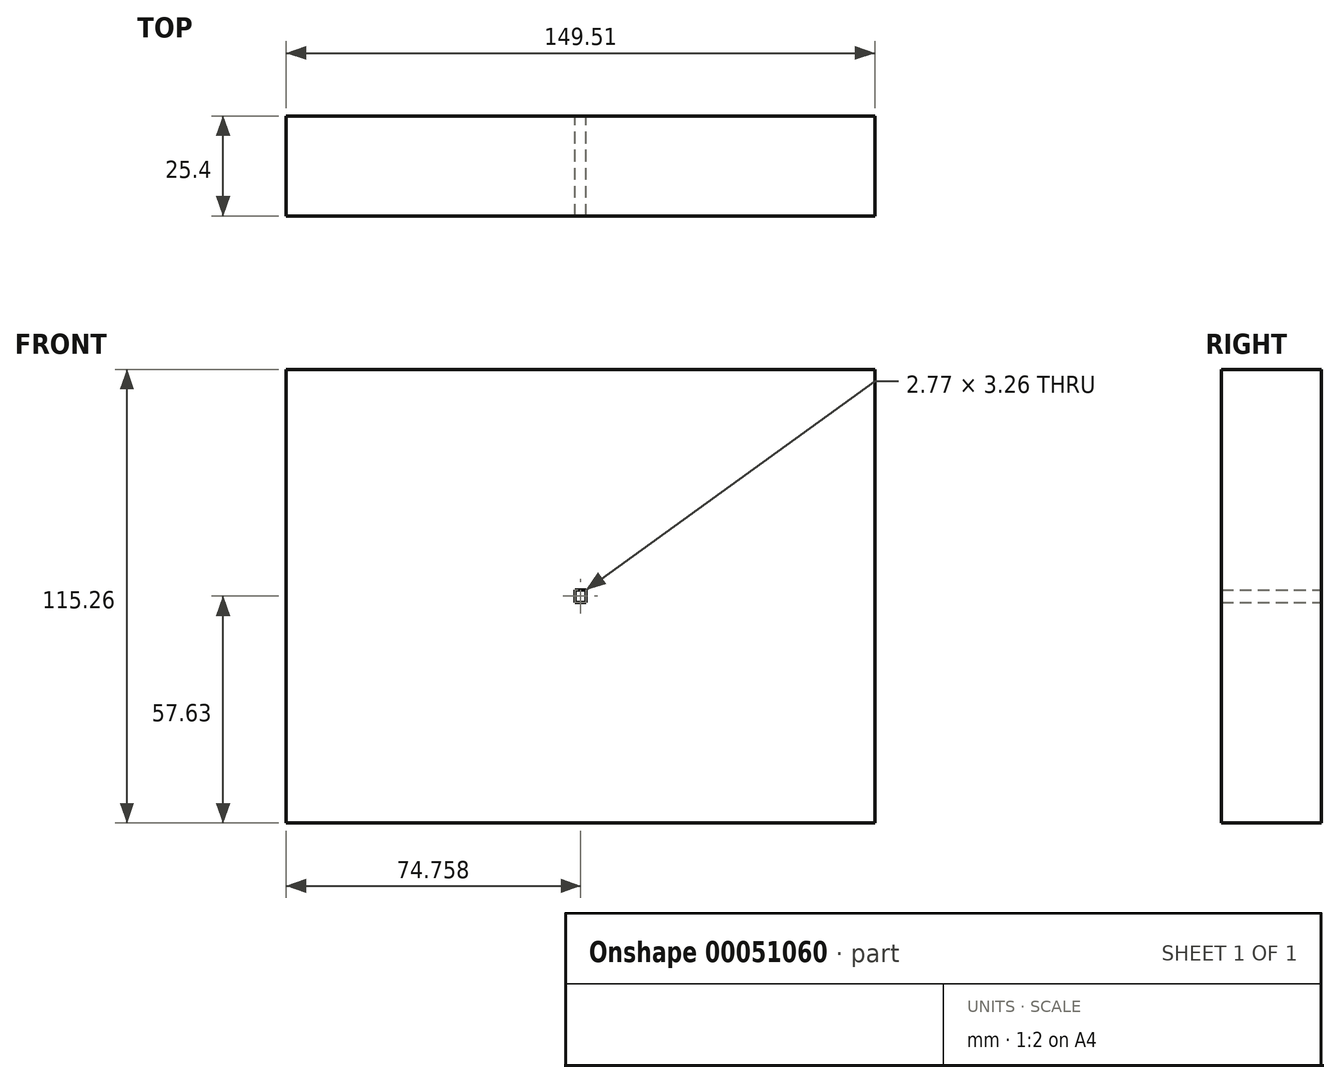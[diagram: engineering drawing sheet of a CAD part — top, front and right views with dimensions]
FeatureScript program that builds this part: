
annotation { "Feature Type Name" : "Feature", "Feature Type Description" : "" }
export const myFeature = defineFeature(function(context is Context, id is Id, definition is map)
    precondition{}
    {
        {
            var Q0;
            Q0=qCreatedBy(makeId("Front.planeOp"),FACE);
            var sketch = newSketch(context, id + "F0", { "sketchPlane" : qUnion([Q0])});
            skLineSegment(sketch, "E0.top", {"start": v(13.5, 0) * mm, "end": v(-11.5, 0) * mm});
            skLineSegment(sketch, "E1.rect.bottom", {"start": v(13.5, -2.63) * mm, "end": v(-16.33, -2.63) * mm});
            skLineSegment(sketch, "E1.rect.top", {"start": v(13.5, -26.63) * mm, "end": v(-16.33, -26.63) * mm});
            skLineSegment(sketch, "E1.rect.left", {"start": v(13.5, -2.63) * mm, "end": v(13.5, -26.63) * mm});
            skLineSegment(sketch, "E1.rect.right", {"start": v(-16.33, -2.63) * mm, "end": v(-16.33, -26.63) * mm});
            skPoint(sketch, "E1.rect.middle", {"position": v(-1.41, -14.63) * mm});
            skLineSegment(sketch, "E2.rect.bottom", {"start": v(20.55, 0) * mm, "end": v(-23.37, 0) * mm});
            skLineSegment(sketch, "E2.rect.top", {"start": v(20.55, -29.26) * mm, "end": v(-23.37, -29.26) * mm});
            skLineSegment(sketch, "E2.rect.left", {"start": v(20.55, 0) * mm, "end": v(20.55, -29.26) * mm});
            skLineSegment(sketch, "E2.rect.right", {"start": v(-23.37, 0) * mm, "end": v(-23.37, -29.26) * mm});
            skLineSegment(sketch, "E3.rect.bottom", {"start": v(34.9, 9.79) * mm, "end": v(-37.73, 9.79) * mm});
            skLineSegment(sketch, "E3.rect.top", {"start": v(34.9, -39.05) * mm, "end": v(-37.73, -39.05) * mm});
            skLineSegment(sketch, "E3.rect.left", {"start": v(34.9, 9.79) * mm, "end": v(34.9, -39.05) * mm});
            skLineSegment(sketch, "E3.rect.right", {"start": v(-37.73, 9.79) * mm, "end": v(-37.73, -39.05) * mm});
            skLineSegment(sketch, "E4.rect.bottom", {"start": v(44.2, 15.84) * mm, "end": v(-47.02, 15.84) * mm});
            skLineSegment(sketch, "E4.rect.top", {"start": v(44.2, -45.1) * mm, "end": v(-47.02, -45.1) * mm});
            skLineSegment(sketch, "E4.rect.left", {"start": v(44.2, 15.84) * mm, "end": v(44.2, -45.1) * mm});
            skLineSegment(sketch, "E4.rect.right", {"start": v(-47.02, 15.84) * mm, "end": v(-47.02, -45.1) * mm});
            skLineSegment(sketch, "E5.rect.bottom", {"start": v(53.88, 23.91) * mm, "end": v(-56.7, 23.91) * mm});
            skLineSegment(sketch, "E5.rect.top", {"start": v(53.88, -53.17) * mm, "end": v(-56.7, -53.17) * mm});
            skLineSegment(sketch, "E5.rect.left", {"start": v(53.88, 23.91) * mm, "end": v(53.88, -53.17) * mm});
            skLineSegment(sketch, "E5.rect.right", {"start": v(-56.7, 23.91) * mm, "end": v(-56.7, -53.17) * mm});
            skLineSegment(sketch, "E6.rect.bottom", {"start": v(63.97, 33.2) * mm, "end": v(-66.8, 33.2) * mm});
            skLineSegment(sketch, "E6.rect.top", {"start": v(63.97, -62.45) * mm, "end": v(-66.8, -62.45) * mm});
            skLineSegment(sketch, "E6.rect.left", {"start": v(63.97, 33.2) * mm, "end": v(63.97, -62.45) * mm});
            skLineSegment(sketch, "E6.rect.right", {"start": v(-66.8, 33.2) * mm, "end": v(-66.8, -62.45) * mm});
            skLineSegment(sketch, "E7.rect.bottom", {"start": v(73.34, 43) * mm, "end": v(-76.17, 43) * mm});
            skLineSegment(sketch, "E7.rect.top", {"start": v(73.34, -72.26) * mm, "end": v(-76.17, -72.26) * mm});
            skLineSegment(sketch, "E7.rect.left", {"start": v(73.34, 43) * mm, "end": v(73.34, -72.26) * mm});
            skLineSegment(sketch, "E7.rect.right", {"start": v(-76.17, 43) * mm, "end": v(-76.17, -72.26) * mm});
            skLineSegment(sketch, "E8", {"start": v(-76.17, 43) * mm, "end": v(-23.37, 0) * mm});
            skLineSegment(sketch, "E9", {"start": v(34.9, 9.79) * mm, "end": v(73.34, 43) * mm});
            skLineSegment(sketch, "E10", {"start": v(-23.37, -29.26) * mm, "end": v(-76.17, -72.26) * mm});
            skLineSegment(sketch, "E11", {"start": v(20.55, -29.26) * mm, "end": v(73.34, -72.26) * mm});
            skLineSegment(sketch, "E12", {"start": v(34.9, 9.79) * mm, "end": v(20.55, 0) * mm});
            skLineSegment(sketch, "E13", {"start": v(-23.37, -29.26) * mm, "end": v(-16.33, -26.63) * mm});
            skLineSegment(sketch, "E14", {"start": v(20.55, -29.26) * mm, "end": v(13.5, -26.63) * mm});
            skLineSegment(sketch, "E15", {"start": v(13.5, -2.63) * mm, "end": v(20.55, 0) * mm});
            skLineSegment(sketch, "E16", {"start": v(-16.33, -2.63) * mm, "end": v(-23.37, 0) * mm});
            skLineSegment(sketch, "E17.rect.bottom", {"start": v(5, -8.29) * mm, "end": v(-7.82, -8.29) * mm});
            skLineSegment(sketch, "E17.rect.top", {"start": v(5, -20.97) * mm, "end": v(-7.82, -20.97) * mm});
            skLineSegment(sketch, "E17.rect.left", {"start": v(5, -8.29) * mm, "end": v(5, -20.97) * mm});
            skLineSegment(sketch, "E17.rect.right", {"start": v(-7.82, -8.29) * mm, "end": v(-7.82, -20.97) * mm});
            skLineSegment(sketch, "E18", {"start": v(13.5, -26.63) * mm, "end": v(5, -20.97) * mm});
            skLineSegment(sketch, "E19", {"start": v(-16.33, -26.63) * mm, "end": v(-7.82, -20.97) * mm});
            skLineSegment(sketch, "E20", {"start": v(13.5, -2.63) * mm, "end": v(5, -8.29) * mm});
            skLineSegment(sketch, "E21", {"start": v(-1.61, -10.6) * mm, "end": v(-16.33, -2.63) * mm});
            skLineSegment(sketch, "E22.rect.bottom", {"start": v(-0.03, -13) * mm, "end": v(-2.8, -13) * mm});
            skLineSegment(sketch, "E22.rect.top", {"start": v(-0.03, -16.26) * mm, "end": v(-2.8, -16.26) * mm});
            skLineSegment(sketch, "E22.rect.left", {"start": v(-0.03, -13) * mm, "end": v(-0.03, -16.26) * mm});
            skLineSegment(sketch, "E22.rect.right", {"start": v(-2.8, -13) * mm, "end": v(-2.8, -16.26) * mm});
            skLineSegment(sketch, "E23", {"start": v(5, -20.97) * mm, "end": v(-0.03, -16.26) * mm});
            skLineSegment(sketch, "E24", {"start": v(-7.82, -20.97) * mm, "end": v(-2.8, -16.26) * mm});
            skLineSegment(sketch, "E25", {"start": v(-7.82, -8.29) * mm, "end": v(-2.8, -13) * mm});
            skLineSegment(sketch, "E26", {"start": v(5, -8.29) * mm, "end": v(-0.03, -13) * mm});
            skSolve(sketch);
        }
        {
            var Q0;
            {var subQ1=sQuery(id+"F0.wireOp",EDGE,"E6.rect.right");Q0=makeQuery(id+"F0.imprint","IMPRINT",FACE,{"disambiguationData":[TD([[makeQuery(id+"F0.imprint","IMPRINT",EDGE,{"derivedFrom":subQ1}),-1.0]])]});}
            var Q1;
            {var subQ5=sQuery(id+"F0.wireOp",EDGE,"E7.rect.bottom");Q1=makeQuery(id+"F0.imprint","IMPRINT",FACE,{"disambiguationData":[TD([[makeQuery(id+"F0.imprint","IMPRINT",EDGE,{"derivedFrom":subQ5}),1.0]])]});}
            var Q2;
            {var subQ1=sQuery(id+"F0.wireOp",EDGE,"E6.rect.left");Q2=makeQuery(id+"F0.imprint","IMPRINT",FACE,{"disambiguationData":[TD([[makeQuery(id+"F0.imprint","IMPRINT",EDGE,{"derivedFrom":subQ1}),1.0]])]});}
            var Q3;
            {var subQ5=sQuery(id+"F0.wireOp",EDGE,"E7.rect.top");Q3=makeQuery(id+"F0.imprint","IMPRINT",FACE,{"disambiguationData":[TD([[makeQuery(id+"F0.imprint","IMPRINT",EDGE,{"derivedFrom":subQ5}),-1.0]])]});}
            extrude(context, id + "F1", {"entities" : qUnion([Q0, Q1, Q2, Q3]), "depth" : 25.4 * mm});
        }
        {
            var Q0;
            {var subQ4=sQuery(id+"F0.wireOp",EDGE,"E5.rect.right");Q0=makeQuery(id+"F0.imprint","IMPRINT",FACE,{"disambiguationData":[TD([[makeQuery(id+"F0.imprint","IMPRINT",EDGE,{"derivedFrom":subQ4}),-1.0]])]});}
            var Q1;
            {var subQ0=sQuery(id+"F0.wireOp",EDGE,"E9");var subQ1=sQuery(id+"F0.wireOp",EDGE,"E5.rect.bottom");var subQ2=makeQuery(id+"F0.imprint","INTERSECT",VERTEX,{"derivedFrom":[subQ1,subQ0]});Q1=makeQuery(id+"F0.imprint","IMPRINT",FACE,{"disambiguationData":[TD([[makeQuery(id+"F0.imprint","IMPRINT",EDGE,{"disambiguationData":[TD([[subQ2,-1.0]])],"derivedFrom":subQ1}),-1.0]])]});}
            var Q2;
            {var subQ4=sQuery(id+"F0.wireOp",EDGE,"E5.rect.left");Q2=makeQuery(id+"F0.imprint","IMPRINT",FACE,{"disambiguationData":[TD([[makeQuery(id+"F0.imprint","IMPRINT",EDGE,{"derivedFrom":subQ4}),1.0]])]});}
            var Q3;
            {var subQ0=sQuery(id+"F0.wireOp",EDGE,"E11");var subQ1=sQuery(id+"F0.wireOp",EDGE,"E5.rect.top");var subQ2=makeQuery(id+"F0.imprint","INTERSECT",VERTEX,{"derivedFrom":[subQ1,subQ0]});Q3=makeQuery(id+"F0.imprint","IMPRINT",FACE,{"disambiguationData":[TD([[makeQuery(id+"F0.imprint","IMPRINT",EDGE,{"disambiguationData":[TD([[subQ2,-1.0]])],"derivedFrom":subQ1}),1.0]])]});}
            extrude(context, id + "F2", {"entities" : qUnion([Q0, Q1, Q2, Q3]), "operationType" : NewBodyOperationType.ADD, "depth" : 25.4 * mm});
        }
        {
            var Q0;
            {var subQ4=sQuery(id+"F0.wireOp",EDGE,"E4.rect.right");Q0=makeQuery(id+"F0.imprint","IMPRINT",FACE,{"disambiguationData":[TD([[makeQuery(id+"F0.imprint","IMPRINT",EDGE,{"derivedFrom":subQ4}),-1.0]])]});}
            var Q1;
            {var subQ0=sQuery(id+"F0.wireOp",EDGE,"E9");var subQ1=sQuery(id+"F0.wireOp",EDGE,"E4.rect.bottom");var subQ2=makeQuery(id+"F0.imprint","INTERSECT",VERTEX,{"derivedFrom":[subQ1,subQ0]});Q1=makeQuery(id+"F0.imprint","IMPRINT",FACE,{"disambiguationData":[TD([[makeQuery(id+"F0.imprint","IMPRINT",EDGE,{"disambiguationData":[TD([[subQ2,-1.0]])],"derivedFrom":subQ1}),-1.0]])]});}
            var Q2;
            {var subQ4=sQuery(id+"F0.wireOp",EDGE,"E4.rect.left");Q2=makeQuery(id+"F0.imprint","IMPRINT",FACE,{"disambiguationData":[TD([[makeQuery(id+"F0.imprint","IMPRINT",EDGE,{"derivedFrom":subQ4}),1.0]])]});}
            var Q3;
            {var subQ0=sQuery(id+"F0.wireOp",EDGE,"E11");var subQ1=sQuery(id+"F0.wireOp",EDGE,"E4.rect.top");var subQ2=makeQuery(id+"F0.imprint","INTERSECT",VERTEX,{"derivedFrom":[subQ1,subQ0]});Q3=makeQuery(id+"F0.imprint","IMPRINT",FACE,{"disambiguationData":[TD([[makeQuery(id+"F0.imprint","IMPRINT",EDGE,{"disambiguationData":[TD([[subQ2,-1.0]])],"derivedFrom":subQ1}),1.0]])]});}
            extrude(context, id + "F3", {"entities" : qUnion([Q0, Q1, Q2, Q3]), "operationType" : NewBodyOperationType.ADD, "depth" : 25.4 * mm});
        }
        {
            var Q0;
            {var subQ4=sQuery(id+"F0.wireOp",EDGE,"E3.rect.right");Q0=makeQuery(id+"F0.imprint","IMPRINT",FACE,{"disambiguationData":[TD([[makeQuery(id+"F0.imprint","IMPRINT",EDGE,{"derivedFrom":subQ4}),-1.0]])]});}
            var Q1;
            {var subQ0=sQuery(id+"F0.wireOp",EDGE,"E9");var subQ5=sQuery(id+"F0.wireOp",EDGE,"E4.rect.bottom");var subQ6=makeQuery(id+"F0.imprint","INTERSECT",VERTEX,{"derivedFrom":[subQ5,subQ0]});Q1=makeQuery(id+"F0.imprint","IMPRINT",FACE,{"disambiguationData":[TD([[makeQuery(id+"F0.imprint","IMPRINT",EDGE,{"disambiguationData":[TD([[subQ6,-1.0]])],"derivedFrom":subQ5}),1.0]])]});}
            var Q2;
            {var subQ7=sQuery(id+"F0.wireOp",EDGE,"E3.rect.left");Q2=makeQuery(id+"F0.imprint","IMPRINT",FACE,{"disambiguationData":[TD([[makeQuery(id+"F0.imprint","IMPRINT",EDGE,{"derivedFrom":subQ7}),1.0]])]});}
            var Q3;
            {var subQ0=sQuery(id+"F0.wireOp",EDGE,"E11");var subQ1=sQuery(id+"F0.wireOp",EDGE,"E3.rect.top");var subQ2=makeQuery(id+"F0.imprint","INTERSECT",VERTEX,{"derivedFrom":[subQ1,subQ0]});Q3=makeQuery(id+"F0.imprint","IMPRINT",FACE,{"disambiguationData":[TD([[makeQuery(id+"F0.imprint","IMPRINT",EDGE,{"disambiguationData":[TD([[subQ2,-1.0]])],"derivedFrom":subQ1}),1.0]])]});}
            extrude(context, id + "F4", {"entities" : qUnion([Q0, Q1, Q2, Q3]), "operationType" : NewBodyOperationType.ADD, "depth" : 25.4 * mm});
        }
        {
            var Q0;
            {var subQ7=sQuery(id+"F0.wireOp",EDGE,"E2.rect.right");Q0=makeQuery(id+"F0.imprint","IMPRINT",FACE,{"disambiguationData":[TD([[makeQuery(id+"F0.imprint","IMPRINT",EDGE,{"derivedFrom":subQ7}),-1.0]])]});}
            var Q1;
            {var subQ0=sQuery(id+"F0.wireOp",EDGE,"E12");Q1=makeQuery(id+"F0.imprint","IMPRINT",FACE,{"disambiguationData":[TD([[makeQuery(id+"F0.imprint","IMPRINT",EDGE,{"derivedFrom":subQ0}),-1.0]])]});}
            var Q2;
            {var subQ1=sQuery(id+"F0.wireOp",EDGE,"E2.rect.left");Q2=makeQuery(id+"F0.imprint","IMPRINT",FACE,{"disambiguationData":[TD([[makeQuery(id+"F0.imprint","IMPRINT",EDGE,{"derivedFrom":subQ1}),1.0]])]});}
            var Q3;
            {var subQ0=sQuery(id+"F0.wireOp",EDGE,"E2.rect.top");Q3=makeQuery(id+"F0.imprint","IMPRINT",FACE,{"disambiguationData":[TD([[makeQuery(id+"F0.imprint","IMPRINT",EDGE,{"derivedFrom":subQ0}),1.0]])]});}
            extrude(context, id + "F5", {"entities" : qUnion([Q0, Q1, Q2, Q3]), "operationType" : NewBodyOperationType.ADD, "depth" : 25.4 * mm});
        }
        {
            var Q0;
            Q0=makeQuery(id+"F0.imprint","IMPRINT",FACE,{"disambiguationData":[TD([[makeQuery(id+"F0.imprint","IMPRINT",EDGE,{"derivedFrom":sQuery(id+"F0.wireOp",EDGE,"E1.rect.right")}),-1.0]])]});
            var Q1;
            Q1=makeQuery(id+"F0.imprint","IMPRINT",FACE,{"disambiguationData":[TD([[makeQuery(id+"F0.imprint","IMPRINT",EDGE,{"derivedFrom":sQuery(id+"F0.wireOp",EDGE,"E1.rect.bottom")}),-1.0]])]});
            var Q2;
            Q2=makeQuery(id+"F0.imprint","IMPRINT",FACE,{"disambiguationData":[TD([[makeQuery(id+"F0.imprint","IMPRINT",EDGE,{"derivedFrom":sQuery(id+"F0.wireOp",EDGE,"E1.rect.left")}),1.0]])]});
            var Q3;
            Q3=makeQuery(id+"F0.imprint","IMPRINT",FACE,{"disambiguationData":[TD([[makeQuery(id+"F0.imprint","IMPRINT",EDGE,{"derivedFrom":sQuery(id+"F0.wireOp",EDGE,"E1.rect.top")}),1.0]])]});
            extrude(context, id + "F6", {"entities" : qUnion([Q0, Q1, Q2, Q3]), "operationType" : NewBodyOperationType.ADD, "depth" : 25.4 * mm});
        }
        {
            var Q0;
            Q0=makeQuery(id+"F0.imprint","IMPRINT",FACE,{"disambiguationData":[TD([[makeQuery(id+"F0.imprint","IMPRINT",EDGE,{"derivedFrom":sQuery(id+"F0.wireOp",EDGE,"E1.rect.right")}),1.0]])]});
            var Q1;
            Q1=makeQuery(id+"F0.imprint","IMPRINT",FACE,{"disambiguationData":[TD([[makeQuery(id+"F0.imprint","IMPRINT",EDGE,{"derivedFrom":sQuery(id+"F0.wireOp",EDGE,"E1.rect.bottom")}),1.0]])]});
            var Q2;
            Q2=makeQuery(id+"F0.imprint","IMPRINT",FACE,{"disambiguationData":[TD([[makeQuery(id+"F0.imprint","IMPRINT",EDGE,{"derivedFrom":sQuery(id+"F0.wireOp",EDGE,"E1.rect.left")}),-1.0]])]});
            var Q3;
            Q3=makeQuery(id+"F0.imprint","IMPRINT",FACE,{"disambiguationData":[TD([[makeQuery(id+"F0.imprint","IMPRINT",EDGE,{"derivedFrom":sQuery(id+"F0.wireOp",EDGE,"E1.rect.top")}),-1.0]])]});
            extrude(context, id + "F7", {"entities" : qUnion([Q0, Q1, Q2, Q3]), "operationType" : NewBodyOperationType.ADD, "depth" : 25.4 * mm});
        }
        {
            var Q0;
            Q0=makeQuery(id+"F0.imprint","IMPRINT",FACE,{"disambiguationData":[TD([[makeQuery(id+"F0.imprint","IMPRINT",EDGE,{"derivedFrom":sQuery(id+"F0.wireOp",EDGE,"E17.rect.top")}),-1.0]])]});
            var Q1;
            Q1=makeQuery(id+"F0.imprint","IMPRINT",FACE,{"disambiguationData":[TD([[makeQuery(id+"F0.imprint","IMPRINT",EDGE,{"derivedFrom":sQuery(id+"F0.wireOp",EDGE,"E17.rect.right")}),1.0]])]});
            var Q2;
            Q2=makeQuery(id+"F0.imprint","IMPRINT",FACE,{"disambiguationData":[TD([[makeQuery(id+"F0.imprint","IMPRINT",EDGE,{"derivedFrom":sQuery(id+"F0.wireOp",EDGE,"E17.rect.bottom")}),1.0]])]});
            var Q3;
            Q3=makeQuery(id+"F0.imprint","IMPRINT",FACE,{"disambiguationData":[TD([[makeQuery(id+"F0.imprint","IMPRINT",EDGE,{"derivedFrom":sQuery(id+"F0.wireOp",EDGE,"E17.rect.left")}),-1.0]])]});
            extrude(context, id + "F8", {"entities" : qUnion([Q0, Q1, Q2, Q3]), "operationType" : NewBodyOperationType.ADD, "depth" : 25.4 * mm});
        }
    });
